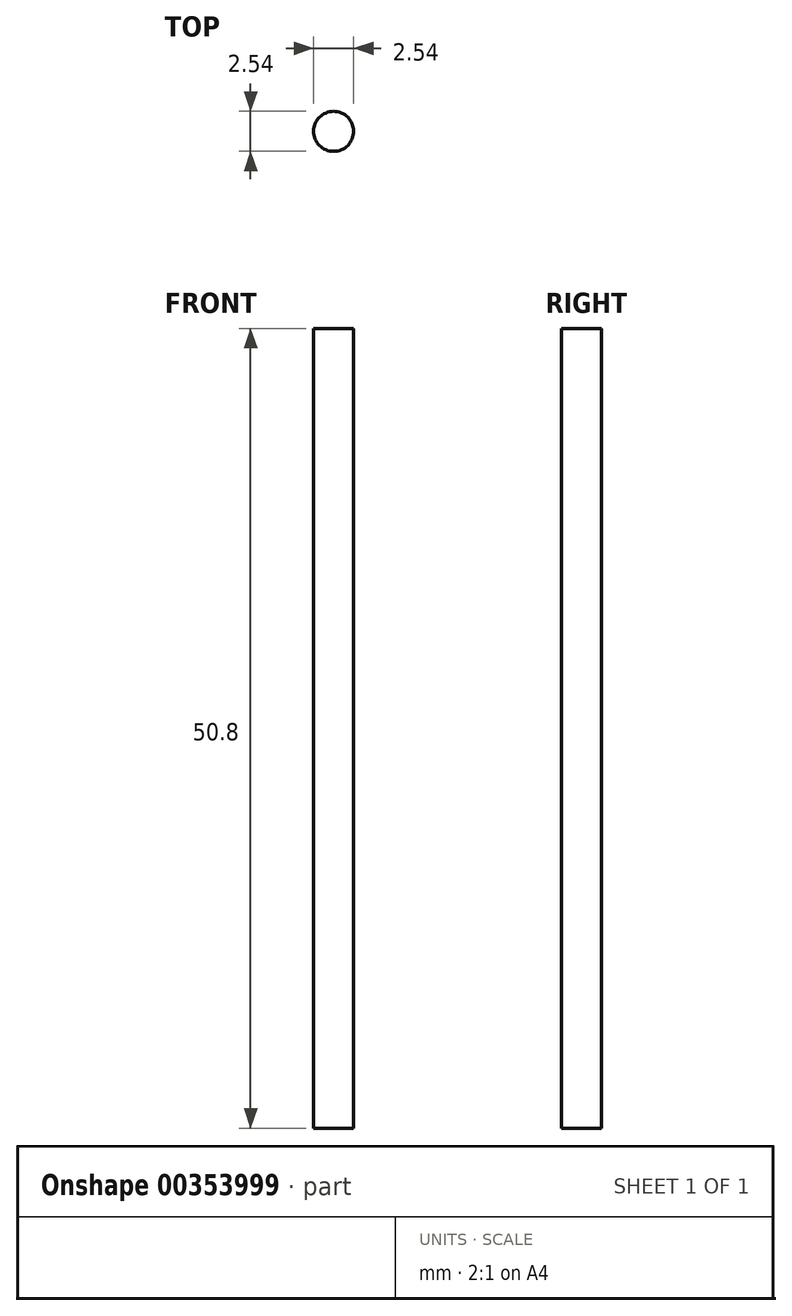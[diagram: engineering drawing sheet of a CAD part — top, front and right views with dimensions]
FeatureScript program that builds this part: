
annotation { "Feature Type Name" : "Feature", "Feature Type Description" : "" }
export const myFeature = defineFeature(function(context is Context, id is Id, definition is map)
    precondition{}
    {
        {
            var Q0;
            Q0=qCreatedBy(makeId("Top.planeOp"),FACE);
            var sketch = newSketch(context, id + "F0", { "sketchPlane" : qUnion([Q0])});
            skCircle(sketch, "E0", {"center": v(0, 0) * mm, "radius": 1.27 * mm});
            skSolve(sketch);
        }
        {
            var Q0;
            Q0 = qSketchRegion(id + "F0", true);
            extrude(context, id + "F1", {"entities" : qUnion([Q0]), "depth" : 50.8 * mm});
        }
    });
